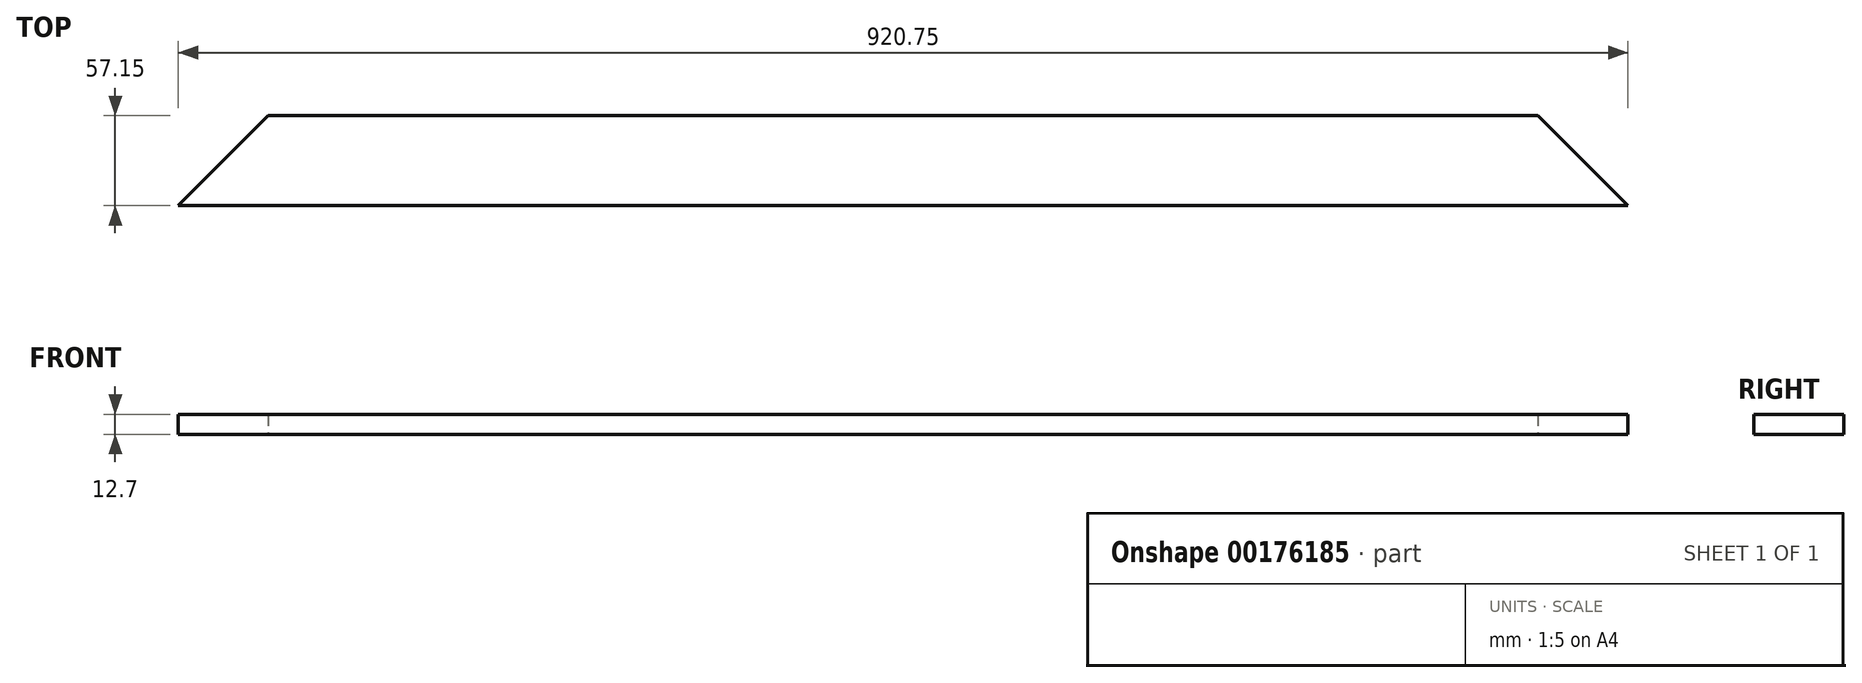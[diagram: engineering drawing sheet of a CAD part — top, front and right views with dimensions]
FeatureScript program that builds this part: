
annotation { "Feature Type Name" : "Feature", "Feature Type Description" : "" }
export const myFeature = defineFeature(function(context is Context, id is Id, definition is map)
    precondition{}
    {
        {
            var Q0;
            Q0=qCreatedBy(makeId("Top.planeOp"),FACE);
            var sketch = newSketch(context, id + "F0", { "sketchPlane" : qUnion([Q0])});
            skLineSegment(sketch, "E0.bottom", {"start": v(0, 0) * mm, "end": v(920.75, 0) * mm});
            skLineSegment(sketch, "E0.top", {"start": v(57.15, 57.15) * mm, "end": v(863.6, 57.15) * mm});
            skLineSegment(sketch, "E1", {"start": v(0, 0) * mm, "end": v(57.15, 57.15) * mm});
            skLineSegment(sketch, "E2", {"start": v(920.75, 0) * mm, "end": v(863.6, 57.15) * mm});
            skSolve(sketch);
        }
        {
            var Q0;
            Q0=makeQuery(id+"F0.imprint","IMPRINT",FACE,{"disambiguationData":[TD([[makeQuery(id+"F0.imprint","IMPRINT",EDGE,{"derivedFrom":sQuery(id+"F0.wireOp",EDGE,"E0.bottom")}),1.0]])]});
            extrude(context, id + "F1", {"entities" : qUnion([Q0]), "depth" : 12.7 * mm});
        }
    });
